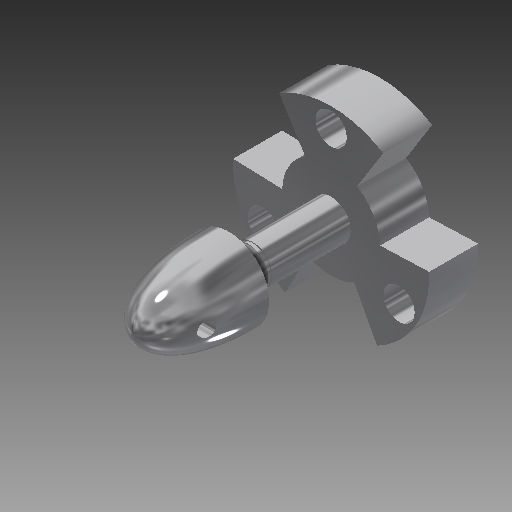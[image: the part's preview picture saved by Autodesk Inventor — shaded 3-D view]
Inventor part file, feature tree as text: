
AUTODESK INVENTOR PART (.ipt)
format: ipt  version: 2019 (Build 230136000, 136)  size: 249,856 bytes
history: native  units: mm
features: sketch x9, extrude x8, reference x5, pattern_circular x1, thread x1, chamfer x1, revolve x1
ambient origin geometry x8: Origin, YZ Plane, XZ Plane, XY Plane, X Axis, Y Axis, Z Axis, Center Point
bodies: Solid1 (feature_tree)
feature tree (26):
  extrude  "Extrusion1"  Depth=20.0mm
  extrude  "Extrusion2"  Depth=5.0mm TaperAngle=0.0deg
  pattern_circular  "Circular Pattern1"  Count=3 Angle=360.0deg
  extrude  "Extrusion3"  Depth=10.0mm TaperAngle=0.0deg
  extrude  "Extrusion4"  Depth=3.2mm
  extrude  "Extrusion5"  Depth=3.0mm TaperAngle=0.0deg
  extrude  "Extrusion6"  Depth=8.0mm TaperAngle=0.0deg
  extrude  "Extrusion7"  Depth=10.0mm TaperAngle=0.0deg
  thread  "Thread1"  [1 undecoded]
  chamfer  "Chamfer1"  Distance=10.0mm
  revolve  "Revolution1"  Angle=45.0deg
  extrude  "Extrusion8"  Depth=8.0mm
  sketch  "Sketch1"  dims[d0=8.0mm d1=20.0mm]
  reference  "Reference1"
  reference  "Reference2"
  reference  "Reference3"
  sketch  "Sketch2"  dims[d2=5.0mm d3=0.0mm d4=5.0mm d5=0.0mm d6=30.0mm d7=360.0deg]
  reference  "Reference4"
  reference  "Reference5"
  sketch  "Sketch3"  dims[d9=10.0mm d10=5.0mm d11=0.0mm]
  sketch  "Sketch4"  dims[d12=3.2mm d13=3.2mm]
  sketch  "Sketch5"  dims[d14=3.2mm d15=3.0mm d16=0.0mm]
  sketch  "Sketch6"  dims[d17=4.0mm d18=8.0mm d19=0.0mm]
  sketch  "Sketch7"  dims[d20=3.8mm d21=0.4mm d22=0.0mm d23=4.0mm d24=10.0mm d25=0.0mm]
  sketch  "Sketch8"  dims[d26=10.0mm d27=0.0mm d28=0.4mm d29=2.0mm d30=45.0deg]
  sketch  "Sketch9"  dims[d31=90.0deg d32=8.0mm d33=9.924142mm d34=1.5mm d35=20.0mm d36=0.0mm]
note: 1 required parameter value undecoded (feature->parameter linkage not recoverable at this tier; creation-order binding heuristic only, values carry confidence <= 0.55)
